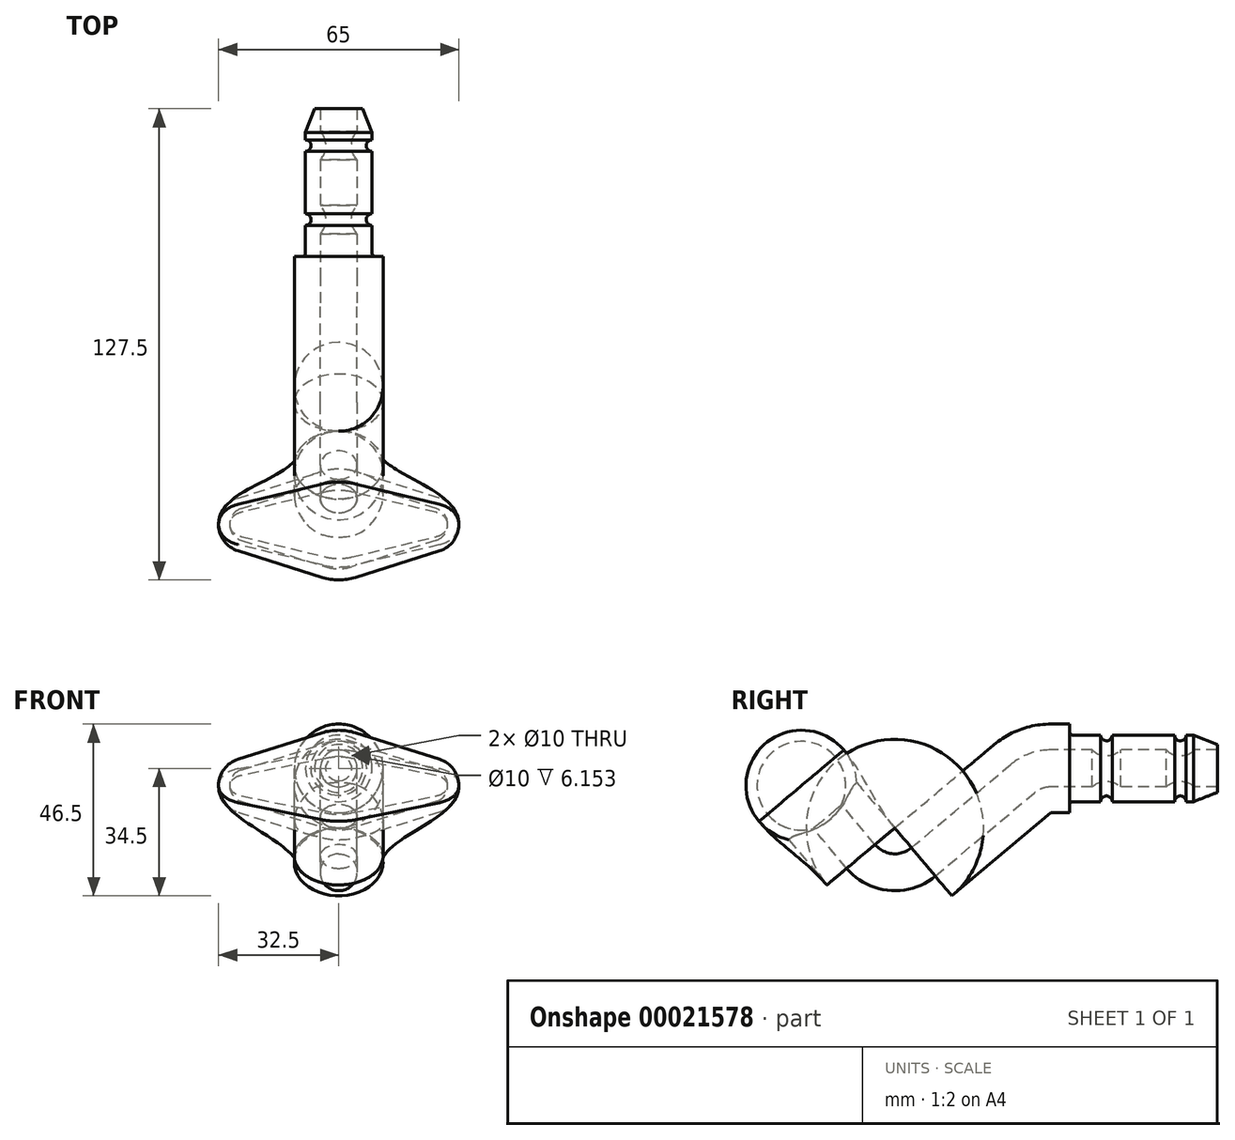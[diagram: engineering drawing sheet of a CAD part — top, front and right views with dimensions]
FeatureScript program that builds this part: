
annotation { "Feature Type Name" : "Feature", "Feature Type Description" : "" }
export const myFeature = defineFeature(function(context is Context, id is Id, definition is map)
    precondition{}
    {
        {
            var Q0;
            Q0=qCreatedBy(makeId("Top.planeOp"),FACE);
            var sketch = newSketch(context, id + "F0", { "sketchPlane" : qUnion([Q0])});
            skLineSegment(sketch, "E0", {"start": v(9, -6.45) * mm, "end": v(9, -8.45) * mm});
            skLineSegment(sketch, "E1", {"start": v(10, -40) * mm, "end": v(12, -40) * mm});
            skLineSegment(sketch, "E2", {"start": v(12, -40) * mm, "end": v(12, -45) * mm});
            skPoint(sketch, "E3.orphan", {"position": v(0, 0) * mm});
            skLineSegment(sketch, "E4", {"start": v(0, -55) * mm, "end": v(0, 0) * mm, "construction": true});
            skArc(sketch, "E5", {"start": v(9, -8.45) * mm, "mid": v(7.45, -10) * mm, "end": v(9, -11.55) * mm});
            skArc(sketch, "E6", {"start": v(9, -28.45) * mm, "mid": v(7.45, -30) * mm, "end": v(9, -31.55) * mm});
            skLineSegment(sketch, "E7.trimOffspring", {"start": v(9, -11.55) * mm, "end": v(9, -28.45) * mm});
            skLineSegment(sketch, "E8.trimOffspring", {"start": v(9, -31.55) * mm, "end": v(9, -39) * mm});
            skLineSegment(sketch, "E9.0", {"start": v(5, -33.85) * mm, "end": v(5, -45) * mm});
            skLineSegment(sketch, "E9.1", {"start": v(5, 0) * mm, "end": v(5, -6.15) * mm});
            skArc(sketch, "E9.2", {"start": v(5, -6.15) * mm, "mid": v(3.45, -10) * mm, "end": v(5, -13.85) * mm});
            skLineSegment(sketch, "E9.3", {"start": v(5, -13.85) * mm, "end": v(5, -26.15) * mm});
            skArc(sketch, "E9.4", {"start": v(5, -26.15) * mm, "mid": v(3.45, -30) * mm, "end": v(5, -33.85) * mm});
            skLineSegment(sketch, "E10", {"start": v(6.5, 0) * mm, "end": v(5, 0) * mm});
            skPoint(sketch, "E11.visualSharp", {"position": v(9, 0) * mm});
            skPoint(sketch, "E12.visualSharp", {"position": v(9, -40) * mm});
            skArc(sketch, "E12.filletArc", {"start": v(9, -39) * mm, "mid": v(9.3, -39.7) * mm, "end": v(10, -40) * mm});
            skLineSegment(sketch, "E13", {"start": v(6.5, 0) * mm, "end": v(9, -6.45) * mm});
            skLineSegment(sketch, "E14", {"start": v(12, -45) * mm, "end": v(5, -45) * mm});
            skSolve(sketch);
        }
        {
            var Q0;
            Q0=qSketchRegion(id+"F0",true);
            var Q1;
            Q1=sQuery(id+"F0.wireOp",EDGE,"E4");
            revolve(context, id + "F1", {"entities" : qUnion([Q0]), "axis" : qUnion([Q1]), "revolveType" : RevolveType.FULL});
        }
        {
            var Q0;
            Q0=qCreatedBy(makeId("Right.planeOp"),FACE);
            var sketch = newSketch(context, id + "F2", { "sketchPlane" : qUnion([Q0])});
            skLineSegment(sketch, "E15", {"start": v(0, 0) * mm, "end": v(-45, 0) * mm});
            skLineSegment(sketch, "E16", {"start": v(-45, 0) * mm, "end": v(-79.65, -29.07) * mm});
            skLineSegment(sketch, "E17.0", {"start": v(-45, -12) * mm, "end": v(-45, 12) * mm});
            skSolve(sketch);
        }
        {
            var Q0;
            Q0=qCreatedBy(makeId("Top.planeOp"),FACE);
            var Q1;
            Q1=sQuery(id+"F2.wireOp",EDGE,"E16");
            cPlane(context, id + "F3", {"entities" : qUnion([Q0, Q1]), "cplaneType" : CPlaneType.LINE_ANGLE, "offset" : 25 * mm, "angle" : 0 * degree, "width" : 150 * mm, "height" : 150 * mm});
        }
        {
            var Q0;
            Q0=qCreatedBy(id+"F3.planeOp",FACE);
            var Q1;
            Q1=sQuery(id+"F2.wireOp",VERTEX,"E17.0.start");
            cPlane(context, id + "F4", {"entities" : qUnion([Q0, Q1]), "cplaneType" : CPlaneType.PLANE_POINT, "offset" : 25 * mm, "width" : 150 * mm, "height" : 150 * mm});
        }
        {
            var Q0;
            Q0=qCreatedBy(id+"F4.planeOp",FACE);
            var sketch = newSketch(context, id + "F5", { "sketchPlane" : qUnion([Q0])});
            skLineSegment(sketch, "E18", {"start": v(-11, 42.19) * mm, "end": v(11, 42.19) * mm});
            skSolve(sketch);
        }
        {
            var Q0;
            Q0=makeQuery(id+"F1.opRevolve","SWEPT_FACE",FACE,{"disambiguationData":[OSD([sQuery(id+"F0.wireOp",EDGE,"E14")])]});
            cPlane(context, id + "F6", {"entities" : qUnion([Q0]), "cplaneType" : CPlaneType.OFFSET, "offset" : 0 * mm, "width" : 150 * mm, "height" : 150 * mm});
        }
        {
            var Q0;
            Q0=qCreatedBy(id+"F6.planeOp",FACE);
            var Q1;
            Q1=sQuery(id+"F5.wireOp",EDGE,"E18");
            cPlane(context, id + "F7", {"entities" : qUnion([Q0, Q1]), "cplaneType" : CPlaneType.LINE_ANGLE, "offset" : 25 * mm, "angle" : 40 * degree, "width" : 150 * mm, "height" : 150 * mm});
        }
        {
            var Q0;
            Q0=qCreatedBy(id+"F7.planeOp",FACE);
            var sketch = newSketch(context, id + "F8", { "sketchPlane" : qUnion([Q0])});
            skCircle(sketch, "E19", {"center": v(0, 31.73) * mm, "radius": 12 * mm});
            skCircle(sketch, "E20", {"center": v(0, 31.73) * mm, "radius": 5 * mm});
            skSolve(sketch);
        }
        {
            var Q0;
            Q0=makeQuery(id+"F8.imprint","IMPRINT",FACE,{"disambiguationData":[TD([[makeQuery(id+"F8.imprint","IMPRINT",EDGE,{"derivedFrom":sQuery(id+"F8.wireOp",EDGE,"E19")}),1.0]])]});
            extrude(context, id + "F9", {"entities" : qUnion([Q0]), "oppositeDirection" : true, "depth" : 35 * mm});
        }
        {
            var Q0;
            Q0=makeQuery(id+"F9.opExtrude","CAP_FACE",FACE,{"disambiguationData":[OSD([sQuery(id+"F8.wireOp",EDGE,"E19"),sQuery(id+"F8.wireOp",EDGE,"E20")])],"isStart":true});
            var Q1;
            Q1=sQuery(id+"F5.wireOp",EDGE,"E18");
            revolve(context, id + "F10", {"operationType" : NewBodyOperationType.ADD, "entities" : qUnion([Q0]), "axis" : qUnion([Q1]), "revolveType" : RevolveType.ONE_DIRECTION, "oppositeDirection" : true, "angle" : 40 * degree});
        }
        {
            var Q0;
            Q0=makeQuery(id+"F9.opExtrude","CAP_FACE",FACE,{"disambiguationData":[OSD([sQuery(id+"F8.wireOp",EDGE,"E19"),sQuery(id+"F8.wireOp",EDGE,"E20")])],"isStart":false});
            var sketch = newSketch(context, id + "F11", { "sketchPlane" : qUnion([Q0])});
            skLineSegment(sketch, "E21", {"start": v(-14.79, 43.73) * mm, "end": v(14.38, 43.73) * mm});
            skSolve(sketch);
        }
        {
            var Q0;
            Q0=makeQuery(id+"F11.imprint","IMPRINT",FACE,{"disambiguationData":[TD([[makeQuery(id+"F11.imprint","IMPRINT",EDGE,{"derivedFrom":makeQuery(id+"F9.opExtrude","CAP_EDGE",EDGE,{"disambiguationData":[OSD([sQuery(id+"F8.wireOp",EDGE,"E19")])],"isStart":false})}),-1.0]])]});
            var Q1;
            Q1=sQuery(id+"F11.wireOp",EDGE,"E21");
            revolve(context, id + "F12", {"operationType" : NewBodyOperationType.ADD, "entities" : qUnion([Q0]), "axis" : qUnion([Q1]), "revolveType" : RevolveType.ONE_DIRECTION, "oppositeDirection" : true, "angle" : 90 * degree});
        }
        {
            var Q0;
            Q0=makeQuery(id+"F12.opRevolve","CAP_FACE",FACE,{"disambiguationData":[OSD([sQuery(id+"F8.wireOp",EDGE,"E19"),sQuery(id+"F8.wireOp",EDGE,"E20")])],"isStart":false});
            cPlane(context, id + "F13", {"entities" : qUnion([Q0]), "cplaneType" : CPlaneType.OFFSET, "offset" : 25 * mm, "width" : 150 * mm, "height" : 150 * mm});
        }
        {
            var Q0;
            Q0=makeQuery(id+"F12.opRevolve","CAP_FACE",FACE,{"disambiguationData":[OSD([sQuery(id+"F8.wireOp",EDGE,"E19"),sQuery(id+"F8.wireOp",EDGE,"E20")])],"isStart":false});
            cPlane(context, id + "F14", {"entities" : qUnion([Q0]), "cplaneType" : CPlaneType.OFFSET, "offset" : 0 * mm, "width" : 150 * mm, "height" : 150 * mm});
        }
        {
            var Q0;
            Q0=qCreatedBy(id+"F13.planeOp",FACE);
            var sketch = newSketch(context, id + "F15", { "sketchPlane" : qUnion([Q0])});
            skLineSegment(sketch, "E22", {"start": v(25, -89.19) * mm, "end": v(-25, -89.19) * mm, "construction": true});
            skCircle(sketch, "E23.0", {"center": v(0, -89.19) * mm, "radius": 5 * mm, "construction": true});
            skArc(sketch, "E24", {"start": v(27.25, -96.34) * mm, "mid": v(31.05, -93.62) * mm, "end": v(32.5, -89.19) * mm});
            skArc(sketch, "E25", {"start": v(-32.5, -89.19) * mm, "mid": v(-31.05, -93.62) * mm, "end": v(-27.25, -96.34) * mm});
            skLineSegment(sketch, "E26", {"start": v(27.25, -96.34) * mm, "end": v(4.5, -103.5) * mm});
            skLineSegment(sketch, "E27", {"start": v(-4.5, -103.5) * mm, "end": v(-27.25, -96.34) * mm});
            skArc(sketch, "E28.trimOffspring", {"start": v(-4.5, -103.5) * mm, "mid": v(0, -104.19) * mm, "end": v(4.5, -103.5) * mm});
            skLineSegment(sketch, "E29", {"start": v(32.5, -89.19) * mm, "end": v(-32.5, -89.19) * mm});
            skLineSegment(sketch, "E30", {"start": v(0, -89.19) * mm, "end": v(0, -104.19) * mm, "construction": true});
            skSolve(sketch);
        }
        {
            var Q0;
            Q0=qSketchRegion(id+"F15",true);
            var Q1;
            Q1=sQuery(id+"F15.wireOp",EDGE,"E29");
            revolve(context, id + "F16", {"entities" : qUnion([Q0]), "axis" : qUnion([Q1]), "revolveType" : RevolveType.FULL});
        }
        {
            var Q0;
            Q0=qCreatedBy(id+"F13.planeOp",FACE);
            var sketch = newSketch(context, id + "F17", { "sketchPlane" : qUnion([Q0])});
            skArc(sketch, "E31", {"start": v(4.37, -91.62) * mm, "mid": v(0, -84.19) * mm, "end": v(-4.37, -91.62) * mm});
            skCircle(sketch, "E32.0", {"center": v(0, -89.19) * mm, "radius": 5 * mm});
            skSolve(sketch);
        }
        {
            var Q0;
            Q0=qSketchRegion(id+"F17",true);
            extrude(context, id + "F18", {"entities" : qUnion([Q0]), "operationType" : NewBodyOperationType.REMOVE, "oppositeDirection" : true, "depth" : 25 * mm});
        }
        {
            var Q0;
            Q0=makeQuery(id+"F12.opRevolve","CAP_FACE",FACE,{"disambiguationData":[OSD([sQuery(id+"F8.wireOp",EDGE,"E19"),sQuery(id+"F8.wireOp",EDGE,"E20")])],"isStart":false});
            var sketch = newSketch(context, id + "F19", { "sketchPlane" : qUnion([Q0])});
            skCircle(sketch, "E33.0", {"center": v(0, -89.19) * mm, "radius": 12 * mm});
            skCircle(sketch, "E34.0", {"center": v(0, -89.19) * mm, "radius": 5 * mm});
            skSolve(sketch);
        }
        {
            var Q0;
            Q0=qSketchRegion(id+"F19",true);
            extrude(context, id + "F20", {"entities" : qUnion([Q0]), "operationType" : NewBodyOperationType.ADD, "endBound" : BoundingType.UP_TO_NEXT, "depth" : 25 * mm});
        }
        {
            var Q0;
            Q0=qCreatedBy(id+"F13.planeOp",FACE);
            var sketch = newSketch(context, id + "F21", { "sketchPlane" : qUnion([Q0])});
            skLineSegment(sketch, "E35", {"start": v(4.5, -74.88) * mm, "end": v(27.25, -82.03) * mm});
            skLineSegment(sketch, "E36", {"start": v(27.25, -96.34) * mm, "end": v(4.5, -103.5) * mm});
            skLineSegment(sketch, "E37", {"start": v(-4.5, -103.5) * mm, "end": v(-27.25, -96.34) * mm});
            skLineSegment(sketch, "E38", {"start": v(-27.25, -82.03) * mm, "end": v(-4.5, -74.88) * mm});
            skArc(sketch, "E39", {"start": v(4.5, -74.88) * mm, "mid": v(0, -74.19) * mm, "end": v(-4.5, -74.88) * mm});
            skArc(sketch, "E40", {"start": v(27.25, -96.34) * mm, "mid": v(32.5, -89.19) * mm, "end": v(27.25, -82.03) * mm});
            skArc(sketch, "E41", {"start": v(-27.25, -82.03) * mm, "mid": v(-32.5, -89.19) * mm, "end": v(-27.25, -96.34) * mm});
            skArc(sketch, "E42.trimOffspring", {"start": v(-4.5, -103.5) * mm, "mid": v(0, -104.19) * mm, "end": v(4.5, -103.5) * mm});
            skSolve(sketch);
        }
        {
            var Q0;
            Q0=qCreatedBy(id+"F14.planeOp",FACE);
            var sketch = newSketch(context, id + "F22", { "sketchPlane" : qUnion([Q0])});
            skCircle(sketch, "E43.0", {"center": v(0, -89.19) * mm, "radius": 12 * mm});
            skSolve(sketch);
        }
        {
            var Q0;
            Q0=makeQuery(id+"F22.imprint","IMPRINT",FACE,{"disambiguationData":[TD([[makeQuery(id+"F22.imprint","IMPRINT",EDGE,{"derivedFrom":sQuery(id+"F22.wireOp",EDGE,"E43.0")}),1.0]])]});
            var Q1;
            Q1=makeQuery(id+"F21.imprint","IMPRINT",FACE,{"disambiguationData":[TD([[makeQuery(id+"F21.imprint","IMPRINT",EDGE,{"derivedFrom":sQuery(id+"F21.wireOp",EDGE,"E35")}),-1.0]])]});
            loft(context, id + "F23", {"startCondition" : LoftEndDerivativeType.NORMAL_TO_PROFILE, "startMagnitude" : 1, "endCondition" : LoftEndDerivativeType.NORMAL_TO_PROFILE, "endMagnitude" : 1, "sheetProfilesArray" : [{ "sheetProfileEntities" : qUnion([Q0]) }, { "sheetProfileEntities" : qUnion([Q1]) }]});
        }
        {
            var Q0;
            Q0=qCreatedBy(id+"F13.planeOp",FACE);
            var sketch = newSketch(context, id + "F24", { "sketchPlane" : qUnion([Q0])});
            skLineSegment(sketch, "E44.0", {"start": v(29.5, -89.19) * mm, "end": v(-29.5, -89.19) * mm});
            skArc(sketch, "E45.0", {"start": v(26.35, -93.48) * mm, "mid": v(28.63, -91.85) * mm, "end": v(29.5, -89.19) * mm});
            skArc(sketch, "E45.1", {"start": v(-29.5, -89.19) * mm, "mid": v(-28.63, -91.85) * mm, "end": v(-26.35, -93.48) * mm});
            skLineSegment(sketch, "E45.2", {"start": v(-3.6, -100.63) * mm, "end": v(-26.35, -93.48) * mm});
            skArc(sketch, "E45.3", {"start": v(-3.6, -100.63) * mm, "mid": v(0, -101.19) * mm, "end": v(3.6, -100.63) * mm});
            skLineSegment(sketch, "E45.4", {"start": v(26.35, -93.48) * mm, "end": v(3.6, -100.63) * mm});
            skPoint(sketch, "E46.orphan", {"position": v(32.5, -89.19) * mm});
            skPoint(sketch, "E47.orphan", {"position": v(-32.5, -89.19) * mm});
            skSolve(sketch);
        }
        {
            var Q0;
            Q0=makeQuery(id+"F24.imprint","IMPRINT",FACE,{"disambiguationData":[TD([[makeQuery(id+"F24.imprint","IMPRINT",EDGE,{"derivedFrom":sQuery(id+"F24.wireOp",EDGE,"E44.0")}),1.0]])]});
            var Q1;
            Q1=sQuery(id+"F24.wireOp",EDGE,"E44.0");
            revolve(context, id + "F25", {"operationType" : NewBodyOperationType.REMOVE, "entities" : qUnion([Q0]), "axis" : qUnion([Q1]), "revolveType" : RevolveType.FULL, "oppositeDirection" : true});
        }
        {
            var Q0;
            Q0 = qSketchRegion(id + "F17", true);
            extrude(context, id + "F26", {"entities" : qUnion([Q0]), "operationType" : NewBodyOperationType.REMOVE, "oppositeDirection" : true, "depth" : 25 * mm});
        }
    });
